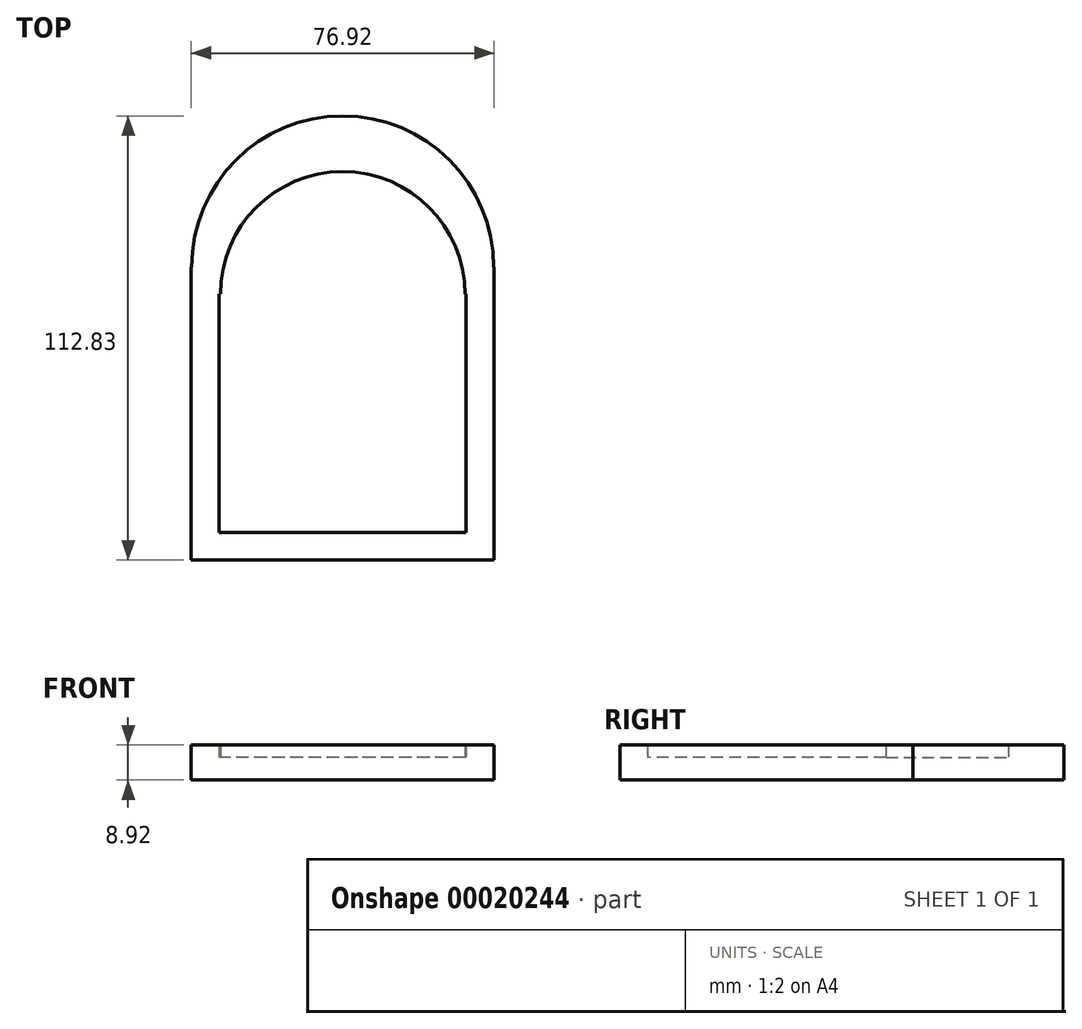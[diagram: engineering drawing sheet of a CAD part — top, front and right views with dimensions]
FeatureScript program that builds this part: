
annotation { "Feature Type Name" : "Feature", "Feature Type Description" : "" }
export const myFeature = defineFeature(function(context is Context, id is Id, definition is map)
    precondition{}
    {
        {
            var Q0;
            Q0=qCreatedBy(makeId("Top.planeOp"),FACE);
            var sketch = newSketch(context, id + "F0", { "sketchPlane" : qUnion([Q0])});
            skLineSegment(sketch, "E0.rect.bottom", {"start": v(38.46, 0) * mm, "end": v(-38.46, 0) * mm});
            skLineSegment(sketch, "E0.rect.top", {"start": v(38.46, -74.48) * mm, "end": v(-38.46, -74.48) * mm});
            skLineSegment(sketch, "E0.rect.left", {"start": v(38.46, 0) * mm, "end": v(38.46, -74.48) * mm});
            skLineSegment(sketch, "E0.rect.right", {"start": v(-38.46, 0) * mm, "end": v(-38.46, -74.48) * mm});
            skPoint(sketch, "E0.rect.middle", {"position": v(0, -37.24) * mm});
            skCircle(sketch, "E1", {"center": v(0, 0) * mm, "radius": 38.35 * mm});
            skLineSegment(sketch, "E2.rect.bottom", {"start": v(31.34, -6.92) * mm, "end": v(-31.34, -6.92) * mm});
            skLineSegment(sketch, "E2.rect.top", {"start": v(31.34, -67.56) * mm, "end": v(-31.34, -67.56) * mm});
            skLineSegment(sketch, "E2.rect.left", {"start": v(31.34, -6.92) * mm, "end": v(31.34, -67.56) * mm});
            skLineSegment(sketch, "E2.rect.right", {"start": v(-31.34, -6.92) * mm, "end": v(-31.34, -67.56) * mm});
            skCircle(sketch, "E3", {"center": v(0, -6.92) * mm, "radius": 31.08 * mm});
            skSolve(sketch);
        }
        {
            var Q0;
            {var subQ0=sQuery(id+"F0.wireOp",EDGE,"E3");var subQ1=sQuery(id+"F0.wireOp",EDGE,"E0.rect.bottom");var subQ3=makeQuery(id+"F0.imprint","INTERSECT",VERTEX,{"disambiguationData":[OD(0.0)],"derivedFrom":[subQ1,subQ0]});Q0=makeQuery(id+"F0.imprint","IMPRINT",FACE,{"disambiguationData":[TD([[makeQuery(id+"F0.imprint","IMPRINT",EDGE,{"disambiguationData":[TD([[subQ3,-1.0]])],"derivedFrom":subQ1}),-1.0]])]});}
            var Q1;
            {var subQ4=sQuery(id+"F0.wireOp",EDGE,"E2.rect.right");var subQ5=sQuery(id+"F0.wireOp",EDGE,"E1");var subQ6=makeQuery(id+"F0.imprint","INTERSECT",VERTEX,{"derivedFrom":[subQ5,subQ4]});Q1=makeQuery(id+"F0.imprint","IMPRINT",FACE,{"disambiguationData":[TD([[makeQuery(id+"F0.imprint","IMPRINT",EDGE,{"disambiguationData":[TD([[subQ6,-1.0]])],"derivedFrom":subQ5}),1.0]])]});}
            var Q2;
            {var subQ3=sQuery(id+"F0.wireOp",EDGE,"E2.rect.top");Q2=makeQuery(id+"F0.imprint","IMPRINT",FACE,{"disambiguationData":[TD([[makeQuery(id+"F0.imprint","IMPRINT",EDGE,{"derivedFrom":subQ3}),-1.0]])]});}
            var Q3;
            {var subQ0=sQuery(id+"F0.wireOp",EDGE,"E3");var subQ1=sQuery(id+"F0.wireOp",EDGE,"E2.rect.bottom");var subQ3=makeQuery(id+"F0.imprint","INTERSECT",VERTEX,{"disambiguationData":[OD(0.0)],"derivedFrom":[subQ1,subQ0]});Q3=makeQuery(id+"F0.imprint","IMPRINT",FACE,{"disambiguationData":[TD([[makeQuery(id+"F0.imprint","IMPRINT",EDGE,{"disambiguationData":[TD([[subQ3,-1.0]])],"derivedFrom":subQ1}),1.0]])]});}
            var Q4;
            {var subQ0=sQuery(id+"F0.wireOp",EDGE,"E3");var subQ3=sQuery(id+"F0.wireOp",EDGE,"E0.rect.bottom");var subQ6=makeQuery(id+"F0.imprint","INTERSECT",VERTEX,{"disambiguationData":[OD(0.0)],"derivedFrom":[subQ3,subQ0]});Q4=makeQuery(id+"F0.imprint","IMPRINT",FACE,{"disambiguationData":[TD([[makeQuery(id+"F0.imprint","IMPRINT",EDGE,{"disambiguationData":[TD([[subQ6,-1.0]])],"derivedFrom":subQ3}),1.0]])]});}
            extrude(context, id + "F1", {"entities" : qUnion([Q0, Q1, Q2, Q3, Q4]), "depth" : 5.7 * mm});
        }
        {
            var Q0;
            {var subQ3=sQuery(id+"F0.wireOp",EDGE,"E0.rect.bottom");var subQ6=sQuery(id+"F0.wireOp",EDGE,"E1");var subQ9=makeQuery(id+"F0.imprint","INTERSECT",VERTEX,{"disambiguationData":[OD(0.0)],"derivedFrom":[subQ3,subQ6]});Q0=makeQuery(id+"F0.imprint","IMPRINT",FACE,{"disambiguationData":[TD([[makeQuery(id+"F0.imprint","IMPRINT",EDGE,{"disambiguationData":[TD([[subQ9,-1.0]])],"derivedFrom":subQ3}),1.0]])]});}
            var Q1;
            {var subQ1=sQuery(id+"F0.wireOp",EDGE,"E0.rect.bottom");var subQ4=sQuery(id+"F0.wireOp",EDGE,"E1");var subQ6=makeQuery(id+"F0.imprint","INTERSECT",VERTEX,{"disambiguationData":[OD(0.0)],"derivedFrom":[subQ1,subQ4]});Q1=makeQuery(id+"F0.imprint","IMPRINT",FACE,{"disambiguationData":[TD([[makeQuery(id+"F0.imprint","IMPRINT",EDGE,{"disambiguationData":[TD([[subQ6,-1.0]])],"derivedFrom":subQ1}),-1.0]])]});}
            var Q2;
            {var subQ3=sQuery(id+"F0.wireOp",EDGE,"E0.rect.bottom");var subQ6=sQuery(id+"F0.wireOp",EDGE,"E1");var subQ9=makeQuery(id+"F0.imprint","INTERSECT",VERTEX,{"disambiguationData":[OD(1.0)],"derivedFrom":[subQ3,subQ6]});Q2=makeQuery(id+"F0.imprint","IMPRINT",FACE,{"disambiguationData":[TD([[makeQuery(id+"F0.imprint","IMPRINT",EDGE,{"disambiguationData":[TD([[subQ9,1.0]])],"derivedFrom":subQ3}),1.0]])]});}
            var Q3;
            Q3=makeQuery(id+"F0.imprint","IMPRINT",FACE,{"disambiguationData":[TD([[makeQuery(id+"F0.imprint","IMPRINT",EDGE,{"derivedFrom":sQuery(id+"F0.wireOp",EDGE,"E0.rect.top")}),-1.0]])]});
            extrude(context, id + "F2", {"entities" : qUnion([Q0, Q1, Q2, Q3]), "operationType" : NewBodyOperationType.ADD, "depth" : 8.92 * mm});
        }
    });
